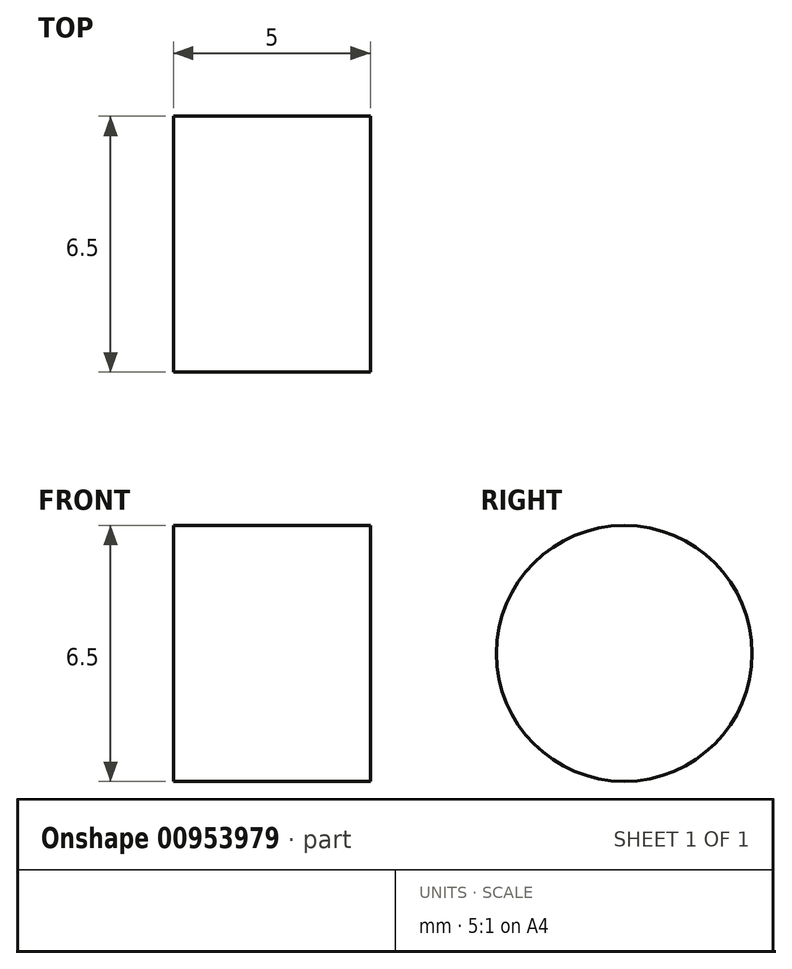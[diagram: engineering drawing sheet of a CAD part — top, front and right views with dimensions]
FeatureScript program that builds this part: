
annotation { "Feature Type Name" : "Feature", "Feature Type Description" : "" }
export const myFeature = defineFeature(function(context is Context, id is Id, definition is map)
    precondition{}
    {
        {
            var Q0;
            Q0=qCreatedBy(makeId("Right.planeOp"),FACE);
            var sketch = newSketch(context, id + "F0", { "sketchPlane" : qUnion([Q0])});
            skCircle(sketch, "E0", {"center": v(0, 0) * mm, "radius": 3.25 * mm});
            skSolve(sketch);
        }
        {
            var Q0;
            Q0 = qSketchRegion(id + "F0", true);
            extrude(context, id + "F1", {"entities" : qUnion([Q0]), "depth" : 5 * mm, "offsetDistance" : 25 * mm});
        }
    });
